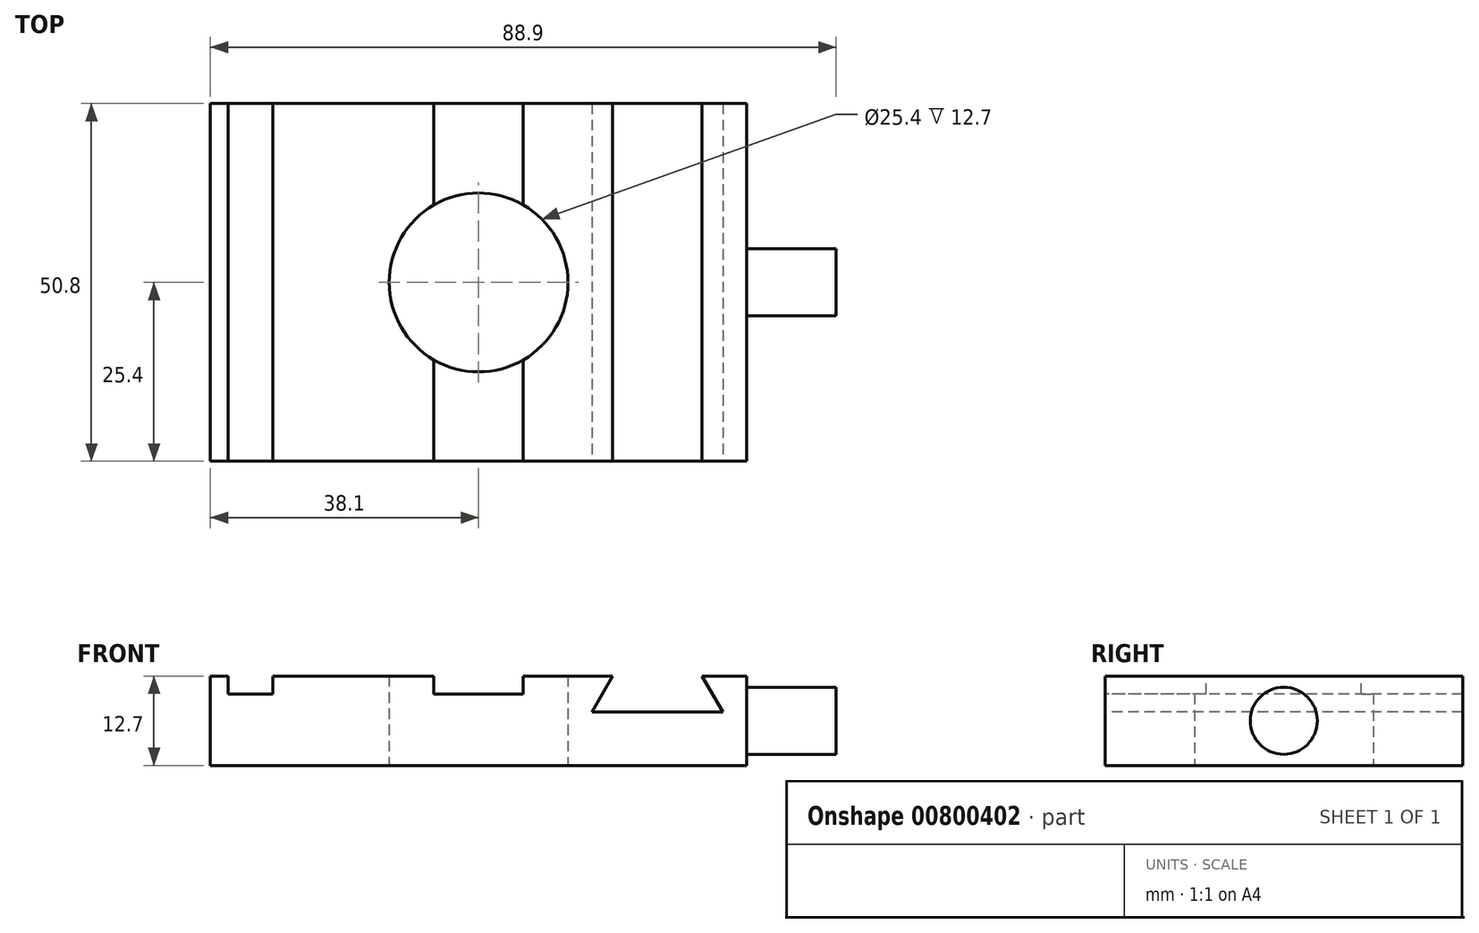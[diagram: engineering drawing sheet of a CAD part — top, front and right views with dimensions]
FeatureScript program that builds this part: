
annotation { "Feature Type Name" : "Feature", "Feature Type Description" : "" }
export const myFeature = defineFeature(function(context is Context, id is Id, definition is map)
    precondition{}
    {
        {
            var Q0;
            Q0=qCreatedBy(makeId("Top.planeOp"),FACE);
            var sketch = newSketch(context, id + "F0", { "sketchPlane" : qUnion([Q0])});
            skLineSegment(sketch, "E0.bottom", {"start": v(38.1, 25.4) * mm, "end": v(-38.1, 25.4) * mm});
            skLineSegment(sketch, "E0.top", {"start": v(38.1, -25.4) * mm, "end": v(-38.1, -25.4) * mm});
            skLineSegment(sketch, "E0.left", {"start": v(38.1, 25.4) * mm, "end": v(38.1, -25.4) * mm});
            skLineSegment(sketch, "E0.right", {"start": v(-38.1, 25.4) * mm, "end": v(-38.1, -25.4) * mm});
            skPoint(sketch, "E0.middle", {"position": v(0, 0) * mm});
            skCircle(sketch, "E1", {"center": v(0, 0) * mm, "radius": 12.7 * mm});
            skSolve(sketch);
        }
        {
            var Q0;
            Q0=makeQuery(id+"F0.imprint","IMPRINT",FACE,{"disambiguationData":[TD([[makeQuery(id+"F0.imprint","IMPRINT",EDGE,{"derivedFrom":sQuery(id+"F0.wireOp",EDGE,"E0.bottom")}),1.0]])]});
            extrude(context, id + "F1", {"entities" : qUnion([Q0]), "depth" : 12.7 * mm, "offsetDistance" : 25.4 * mm});
        }
        {
            var Q0;
            Q0=makeQuery(id+"F1.opExtrude","CAP_FACE",FACE,{"disambiguationData":[OSD([sQuery(id+"F0.wireOp",EDGE,"E0.bottom"),sQuery(id+"F0.wireOp",EDGE,"E0.top"),sQuery(id+"F0.wireOp",EDGE,"E0.left"),sQuery(id+"F0.wireOp",EDGE,"E0.right"),sQuery(id+"F0.wireOp",EDGE,"E1")])],"isStart":false});
            var sketch = newSketch(context, id + "F2", { "sketchPlane" : qUnion([Q0])});
            skLineSegment(sketch, "E2.bottom", {"start": v(-35.56, 25.4) * mm, "end": v(-29.21, 25.4) * mm});
            skLineSegment(sketch, "E2.top", {"start": v(-35.56, -25.4) * mm, "end": v(-29.21, -25.4) * mm});
            skLineSegment(sketch, "E2.left", {"start": v(-35.56, 25.4) * mm, "end": v(-35.56, -25.4) * mm});
            skLineSegment(sketch, "E2.right", {"start": v(-29.21, 25.4) * mm, "end": v(-29.21, -25.4) * mm});
            skLineSegment(sketch, "E3", {"start": v(-6.35, 25.4) * mm, "end": v(-6.35, -25.4) * mm});
            skLineSegment(sketch, "E4", {"start": v(-6.35, -25.4) * mm, "end": v(6.35, -25.4) * mm});
            skLineSegment(sketch, "E5", {"start": v(6.35, -25.4) * mm, "end": v(6.35, 25.4) * mm});
            skLineSegment(sketch, "E6", {"start": v(6.35, 25.4) * mm, "end": v(-6.35, 25.4) * mm});
            skLineSegment(sketch, "E7", {"start": v(0, 25.4) * mm, "end": v(0, -25.4) * mm, "construction": true});
            skSolve(sketch);
        }
        {
            var Q0;
            Q0=makeQuery(id+"F2.imprint","IMPRINT",FACE,{"disambiguationData":[TD([[makeQuery(id+"F2.imprint","IMPRINT",EDGE,{"derivedFrom":sQuery(id+"F2.wireOp",EDGE,"E2.bottom")}),1.0]])]});
            var Q1;
            {var subQ0=sQuery(id+"F2.wireOp",EDGE,"E4");Q1=makeQuery(id+"F2.imprint","IMPRINT",FACE,{"disambiguationData":[TD([[makeQuery(id+"F2.imprint","IMPRINT",EDGE,{"derivedFrom":subQ0}),-1.0]])]});}
            var Q2;
            {var subQ0=sQuery(id+"F2.wireOp",EDGE,"E6");Q2=makeQuery(id+"F2.imprint","IMPRINT",FACE,{"disambiguationData":[TD([[makeQuery(id+"F2.imprint","IMPRINT",EDGE,{"derivedFrom":subQ0}),1.0]])]});}
            extrude(context, id + "F3", {"entities" : qUnion([Q0, Q1, Q2]), "operationType" : NewBodyOperationType.REMOVE, "oppositeDirection" : true, "depth" : 2.54 * mm, "offsetDistance" : 25.4 * mm});
        }
        {
            var Q0;
            Q0=makeQuery(id+"F1.opExtrude","SWEPT_FACE",FACE,{"disambiguationData":[OSD([sQuery(id+"F0.wireOp",EDGE,"E0.top")])]});
            var sketch = newSketch(context, id + "F4", { "sketchPlane" : qUnion([Q0])});
            skLineSegment(sketch, "E8", {"start": v(19.05, 12.7) * mm, "end": v(16.1, 7.6) * mm});
            skLineSegment(sketch, "E9", {"start": v(16.1, 7.6) * mm, "end": v(34.7, 7.6) * mm});
            skLineSegment(sketch, "E10", {"start": v(34.7, 7.6) * mm, "end": v(31.75, 12.7) * mm});
            skLineSegment(sketch, "E11", {"start": v(31.75, 12.7) * mm, "end": v(19.05, 12.7) * mm});
            skLineSegment(sketch, "E12", {"start": v(25.4, 7.6) * mm, "end": v(25.4, 12.7) * mm, "construction": true});
            skSolve(sketch);
        }
        {
            var Q0;
            Q0=makeQuery(id+"F4.imprint","IMPRINT",FACE,{"disambiguationData":[TD([[makeQuery(id+"F4.imprint","IMPRINT",EDGE,{"derivedFrom":sQuery(id+"F4.wireOp",EDGE,"E8")}),1.0]])]});
            extrude(context, id + "F5", {"entities" : qUnion([Q0]), "operationType" : NewBodyOperationType.REMOVE, "endBound" : BoundingType.THROUGH_ALL, "oppositeDirection" : true, "depth" : 25.4 * mm, "offsetDistance" : 25.4 * mm});
        }
        {
            var Q0;
            Q0=makeQuery(id+"F1.opExtrude","SWEPT_FACE",FACE,{"disambiguationData":[OSD([sQuery(id+"F0.wireOp",EDGE,"E0.left")])]});
            var sketch = newSketch(context, id + "F6", { "sketchPlane" : qUnion([Q0])});
            skCircle(sketch, "E13", {"center": v(0, 6.35) * mm, "radius": 4.76 * mm});
            skPoint(sketch, "E13.centerSnap0", {"position": v(-25.4, 6.35) * mm});
            skPoint(sketch, "E13.centerSnap1", {"position": v(0, 12.7) * mm});
            skSolve(sketch);
        }
        {
            var Q0;
            Q0=makeQuery(id+"F6.imprint","IMPRINT",FACE,{"disambiguationData":[TD([[makeQuery(id+"F6.imprint","IMPRINT",EDGE,{"derivedFrom":sQuery(id+"F6.wireOp",EDGE,"E13")}),1.0]])]});
            extrude(context, id + "F7", {"entities" : qUnion([Q0]), "operationType" : NewBodyOperationType.ADD, "depth" : 12.7 * mm, "offsetDistance" : 25.4 * mm});
        }
    });
